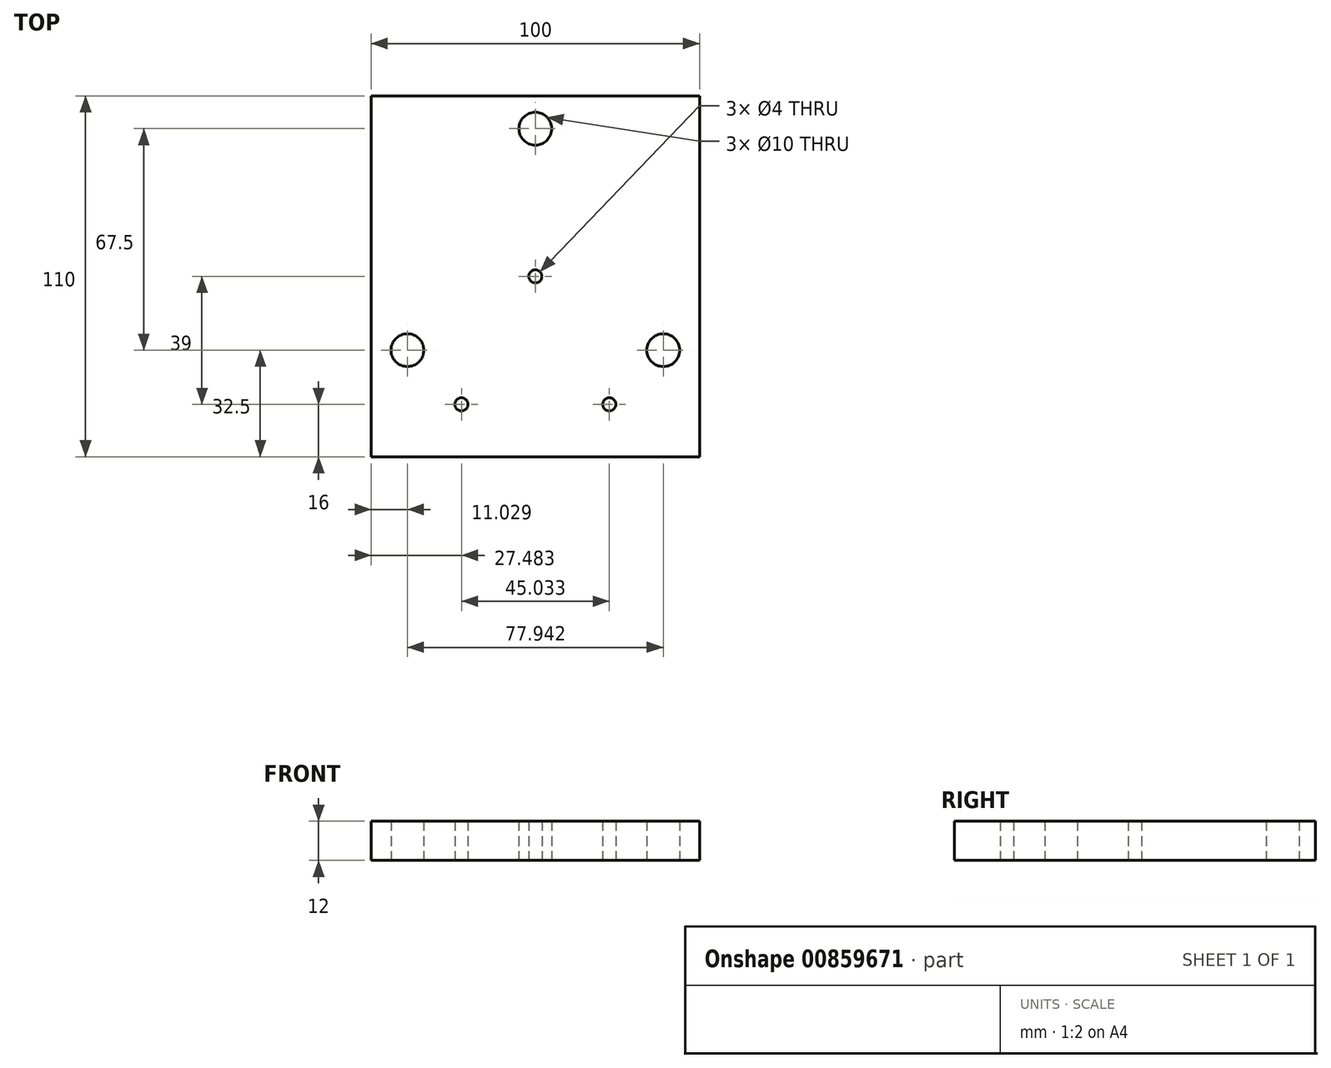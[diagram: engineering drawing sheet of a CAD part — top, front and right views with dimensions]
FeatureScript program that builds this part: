
annotation { "Feature Type Name" : "Feature", "Feature Type Description" : "" }
export const myFeature = defineFeature(function(context is Context, id is Id, definition is map)
    precondition{}
    {
        {
            var Q0;
            Q0=qCreatedBy(makeId("Top.planeOp"),FACE);
            var sketch = newSketch(context, id + "F0", { "sketchPlane" : qUnion([Q0])});
            skCircle(sketch, "E0", {"center": v(0, 0) * mm, "radius": 26 * mm, "construction": true});
            skCircle(sketch, "E1", {"center": v(0, 26) * mm, "radius": 2 * mm});
            skCircle(sketch, "E2", {"center": v(22.52, -13) * mm, "radius": 2 * mm});
            skCircle(sketch, "E3", {"center": v(-22.52, -13) * mm, "radius": 2 * mm});
            skLineSegment(sketch, "E4.bottom", {"start": v(-50, 81) * mm, "end": v(2.75, 81) * mm});
            skLineSegment(sketch, "E4.top", {"start": v(-50, -29) * mm, "end": v(50, -29) * mm});
            skLineSegment(sketch, "E4.left", {"start": v(-50, 81) * mm, "end": v(-50, -29) * mm});
            skLineSegment(sketch, "E4.right", {"start": v(50, 81) * mm, "end": v(50, -29) * mm});
            skCircle(sketch, "E5", {"center": v(0, 26) * mm, "radius": 45 * mm, "construction": true});
            skCircle(sketch, "E6", {"center": v(0, 26) * mm, "radius": 56 * mm, "construction": true});
            skLineSegment(sketch, "E7.trimOffspring", {"start": v(2.75, 81) * mm, "end": v(50, 81) * mm});
            skLineSegment(sketch, "E8", {"start": v(0, 26) * mm, "end": v(0, 82) * mm, "construction": true});
            skLineSegment(sketch, "E9", {"start": v(0, 26) * mm, "end": v(-74.96, -17.28) * mm, "construction": true});
            skLineSegment(sketch, "E10", {"start": v(0, 26) * mm, "end": v(87.43, -24.48) * mm, "construction": true});
            skCircle(sketch, "E11", {"center": v(-38.97, 3.5) * mm, "radius": 5 * mm});
            skCircle(sketch, "E12", {"center": v(38.97, 3.5) * mm, "radius": 5 * mm});
            skCircle(sketch, "E13", {"center": v(0, 71) * mm, "radius": 5 * mm});
            skSolve(sketch);
        }
        {
            var Q0;
            Q0 = qSketchRegion(id + "F0", true);
            extrude(context, id + "F1", {"entities" : qUnion([Q0]), "depth" : 12 * mm, "offsetDistance" : 25 * mm});
        }
    });
